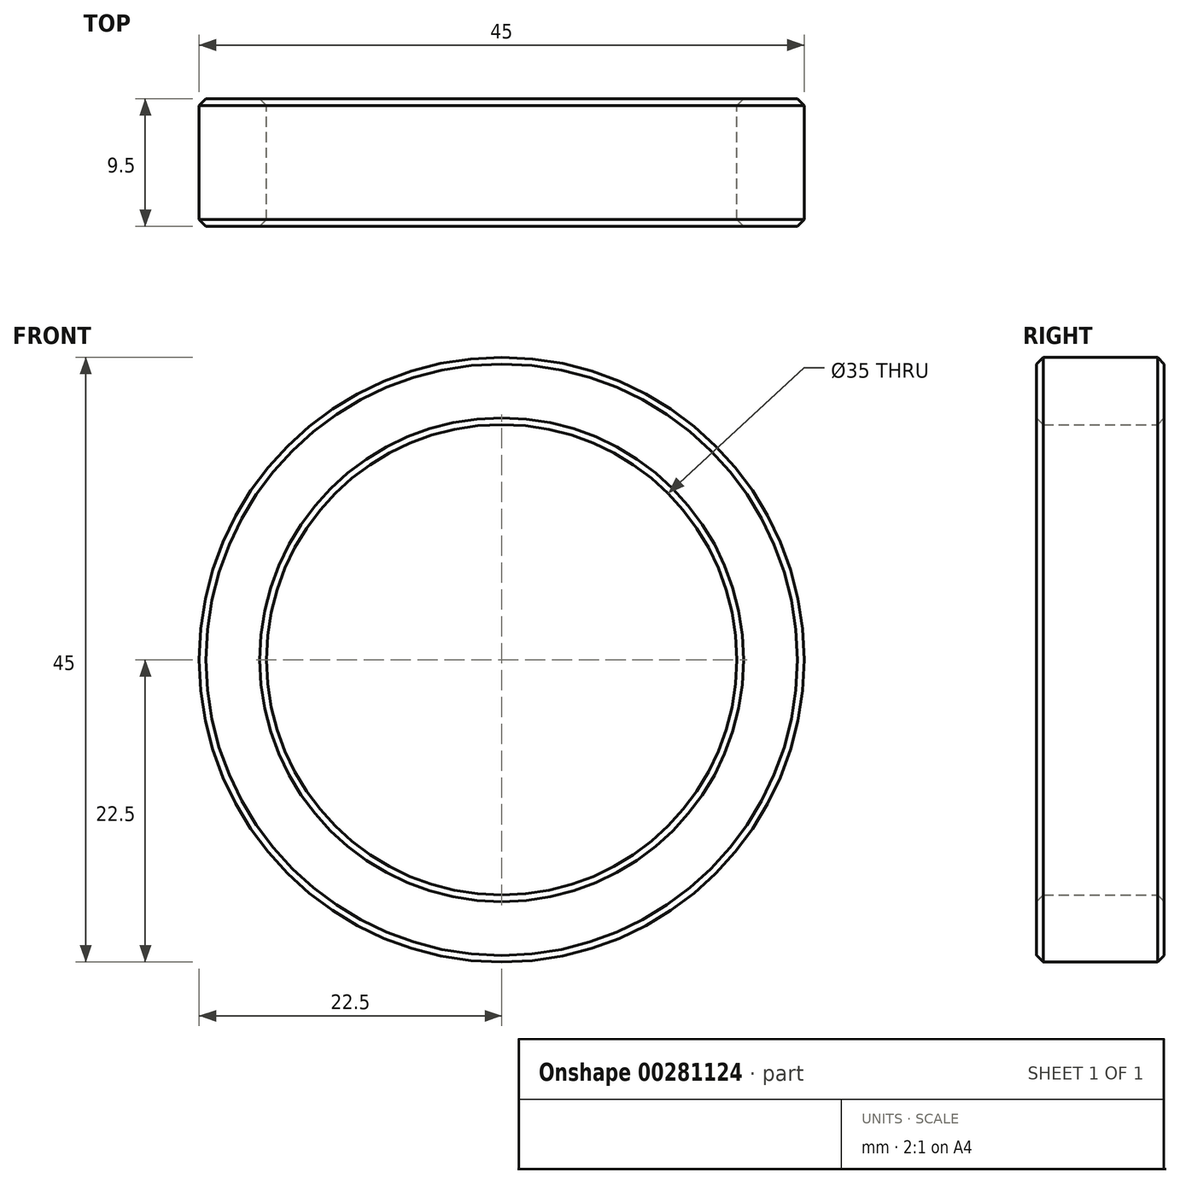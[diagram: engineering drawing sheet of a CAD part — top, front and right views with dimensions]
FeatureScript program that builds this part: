
annotation { "Feature Type Name" : "Feature", "Feature Type Description" : "" }
export const myFeature = defineFeature(function(context is Context, id is Id, definition is map)
    precondition{}
    {
        {
            var Q0;
            Q0=qCreatedBy(makeId("Front.planeOp"),FACE);
            var sketch = newSketch(context, id + "F0", { "sketchPlane" : qUnion([Q0])});
            skCircle(sketch, "E0", {"center": v(0, 0) * mm, "radius": 22.5 * mm});
            skCircle(sketch, "E1", {"center": v(0, 0) * mm, "radius": 17.5 * mm});
            skSolve(sketch);
        }
        {
            var Q0;
            Q0=makeQuery(id+"F0.imprint","IMPRINT",FACE,{"disambiguationData":[TD([[makeQuery(id+"F0.imprint","IMPRINT",EDGE,{"derivedFrom":sQuery(id+"F0.wireOp",EDGE,"E0")}),1.0]])]});
            extrude(context, id + "F1", {"entities" : qUnion([Q0]), "depth" : 9.5 * mm});
        }
        {
            var Q0;
            Q0=makeQuery(id+"F1.opExtrude","CAP_EDGE",EDGE,{"disambiguationData":[OSD([sQuery(id+"F0.wireOp",EDGE,"E0")])],"isStart":false});
            var Q1;
            Q1=makeQuery(id+"F1.opExtrude","CAP_EDGE",EDGE,{"disambiguationData":[OSD([sQuery(id+"F0.wireOp",EDGE,"E1")])],"isStart":false});
            var Q2;
            Q2=makeQuery(id+"F1.opExtrude","CAP_EDGE",EDGE,{"disambiguationData":[OSD([sQuery(id+"F0.wireOp",EDGE,"E0")])],"isStart":true});
            var Q3;
            Q3=makeQuery(id+"F1.opExtrude","CAP_EDGE",EDGE,{"disambiguationData":[OSD([sQuery(id+"F0.wireOp",EDGE,"E1")])],"isStart":true});
            chamfer(context, id + "F2", {"entities" : qUnion([Q0, Q1, Q2, Q3]), "width" : .5 * mm, "tangentPropagation" : true});
        }
    });
